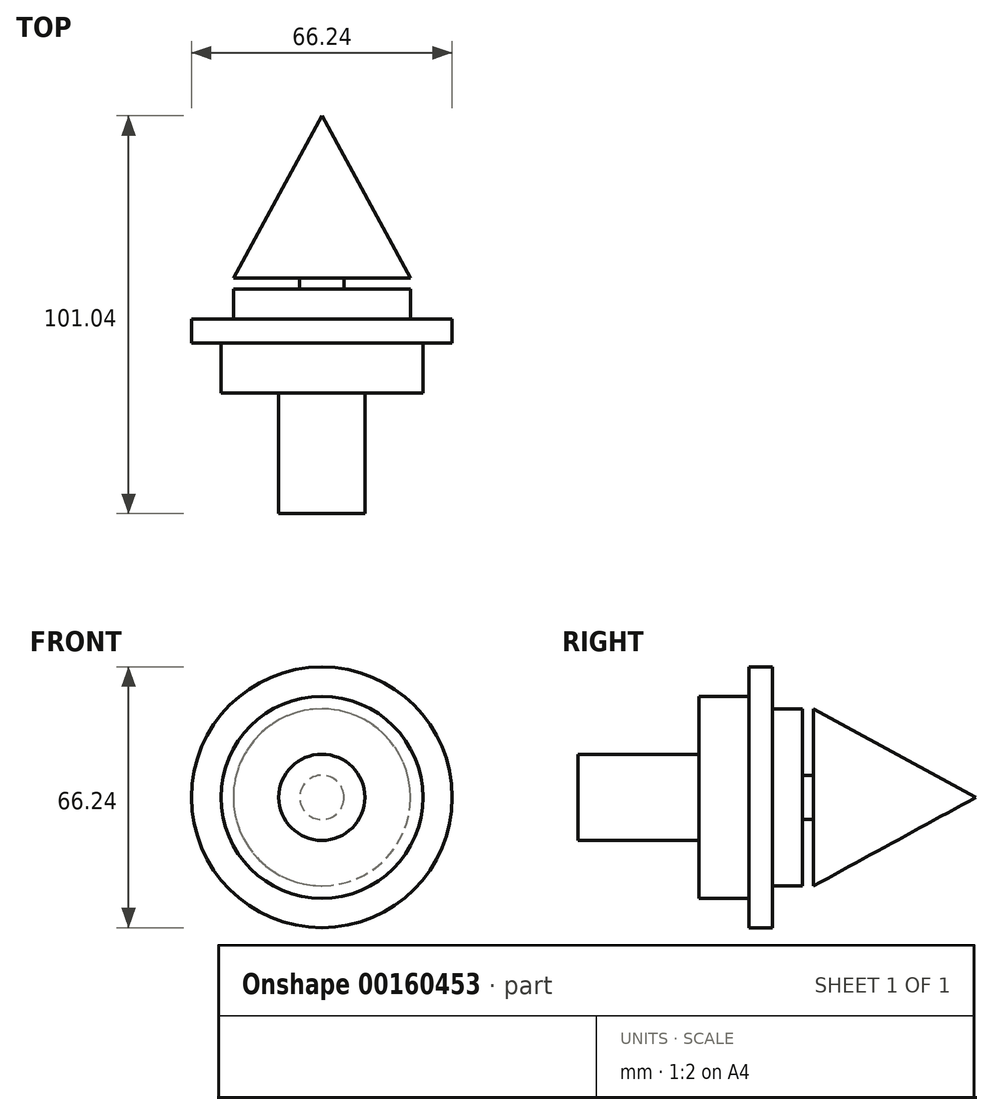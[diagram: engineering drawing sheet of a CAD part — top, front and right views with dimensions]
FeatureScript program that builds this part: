
annotation { "Feature Type Name" : "Feature", "Feature Type Description" : "" }
export const myFeature = defineFeature(function(context is Context, id is Id, definition is map)
    precondition{}
    {
        {
            var Q0;
            Q0=qCreatedBy(makeId("Top.planeOp"),FACE);
            var sketch = newSketch(context, id + "F0", { "sketchPlane" : qUnion([Q0])});
            skLineSegment(sketch, "E0", {"start": v(-33.12, 0) * mm, "end": v(0, 0) * mm});
            skLineSegment(sketch, "E1", {"start": v(-22.5, 0) * mm, "end": v(-22.5, 7.65) * mm});
            skLineSegment(sketch, "E2", {"start": v(-22.5, 7.65) * mm, "end": v(-5.62, 7.65) * mm});
            skLineSegment(sketch, "E3", {"start": v(-5.62, 7.65) * mm, "end": v(-5.62, 10.47) * mm});
            skLineSegment(sketch, "E4", {"start": v(-5.62, 10.47) * mm, "end": v(-22.5, 10.47) * mm});
            skLineSegment(sketch, "E5", {"start": v(-33.12, 0) * mm, "end": v(-33.12, -5.98) * mm});
            skLineSegment(sketch, "E6", {"start": v(-33.12, -5.98) * mm, "end": v(0, -5.98) * mm});
            skLineSegment(sketch, "E7", {"start": v(0, 0) * mm, "end": v(0, -5.98) * mm});
            skPoint(sketch, "E8.MirrorCS.end.orphan", {"position": v(0, -5.98) * mm});
            skPoint(sketch, "E9.orphan", {"position": v(0, 0) * mm});
            skLineSegment(sketch, "E10", {"start": v(-22.5, 10.47) * mm, "end": v(0, 51.7) * mm});
            skLineSegment(sketch, "E11", {"start": v(0, 51.7) * mm, "end": v(0, 0) * mm});
            skSolve(sketch);
        }
        {
            var Q0;
            {var subQ4=sQuery(id+"F0.wireOp",EDGE,"E1");Q0=makeQuery(id+"F0.imprint","IMPRINT",FACE,{"disambiguationData":[TD([[makeQuery(id+"F0.imprint","IMPRINT",EDGE,{"derivedFrom":subQ4}),-1.0]])]});}
            var Q1;
            {var subQ1=sQuery(id+"F0.wireOp",EDGE,"E5");Q1=makeQuery(id+"F0.imprint","IMPRINT",FACE,{"disambiguationData":[TD([[makeQuery(id+"F0.imprint","IMPRINT",EDGE,{"derivedFrom":subQ1}),1.0]])]});}
            var Q2;
            Q2=sQuery(id+"F0.wireOp",EDGE,"E7");
            revolve(context, id + "F1", {"entities" : qUnion([Q0, Q1]), "axis" : qUnion([Q2]), "revolveType" : RevolveType.FULL});
        }
        {
            var Q0;
            Q0=makeQuery(id+"F1.opRevolve","SWEPT_FACE",FACE,{"disambiguationData":[OSD([sQuery(id+"F0.wireOp",EDGE,"E6")])]});
            var sketch = newSketch(context, id + "F2", { "sketchPlane" : qUnion([Q0])});
            skCircle(sketch, "E12", {"center": v(0, 0) * mm, "radius": 10.94 * mm});
            skSolve(sketch);
        }
        {
            var Q0;
            Q0=qCreatedBy(makeId("Top.planeOp"),FACE);
            var sketch = newSketch(context, id + "F3", { "sketchPlane" : qUnion([Q0])});
            skLineSegment(sketch, "E13", {"start": v(0, -6.76) * mm, "end": v(0, -50.12) * mm});
            skSolve(sketch);
        }
        {
            var Q0;
            Q0=makeQuery(id+"F2.imprint","IMPRINT",FACE,{"disambiguationData":[TD([[makeQuery(id+"F2.imprint","IMPRINT",EDGE,{"derivedFrom":sQuery(id+"F2.wireOp",EDGE,"E12")}),1.0]])]});
            var Q1;
            Q1=sQuery(id+"F3.wireOp",EDGE,"E13");
            sweep(context, id + "F4", {"operationType" : NewBodyOperationType.ADD, "profiles" : qUnion([Q0]), "path" : qUnion([Q1])});
        }
        {
            var Q0;
            Q0=makeQuery(id+"F1.opRevolve","SWEPT_FACE",FACE,{"disambiguationData":[OSD([sQuery(id+"F0.wireOp",EDGE,"E6")])]});
            var sketch = newSketch(context, id + "F5", { "sketchPlane" : qUnion([Q0])});
            skCircle(sketch, "E14", {"center": v(0, 0) * mm, "radius": 25.65 * mm});
            skLineSegment(sketch, "E15", {"start": v(0, 25.65) * mm, "end": v(0, 10.94) * mm});
            skLineSegment(sketch, "E16", {"start": v(0, 10.94) * mm, "end": v(10.36, 3.53) * mm});
            skLineSegment(sketch, "E17", {"start": v(0, 10.94) * mm, "end": v(-10.23, 3.88) * mm});
            skLineSegment(sketch, "E18", {"start": v(-10.23, 3.88) * mm, "end": v(-5.38, -9.53) * mm});
            skLineSegment(sketch, "E19", {"start": v(-5.38, -9.53) * mm, "end": v(5.38, -9.53) * mm});
            skLineSegment(sketch, "E20", {"start": v(5.38, -9.53) * mm, "end": v(10.36, 3.53) * mm});
            skSolve(sketch);
        }
        {
            var Q0;
            Q0=makeQuery(id+"F5.imprint","IMPRINT",FACE,{"disambiguationData":[TD([[makeQuery(id+"F5.imprint","IMPRINT",EDGE,{"derivedFrom":sQuery(id+"F5.wireOp",EDGE,"E14")}),1.0]])]});
            extrude(context, id + "F6", {"entities" : qUnion([Q0]), "operationType" : NewBodyOperationType.ADD, "depth" : 12.7 * mm});
        }
        {
            var Q0;
            Q0=sQuery(id+"F5.wireOp",EDGE,"E17");
            var Q1;
            Q1=sQuery(id+"F5.wireOp",EDGE,"E16");
            var Q2;
            Q2=sQuery(id+"F5.wireOp",EDGE,"E20");
            var Q3;
            Q3=sQuery(id+"F5.wireOp",EDGE,"E19");
            var Q4;
            Q4=sQuery(id+"F5.wireOp",EDGE,"E18");
            extrude(context, id + "F7", {"bodyType" : ToolBodyType.SURFACE, "surfaceEntities" : qUnion([Q0, Q1, Q2, Q3, Q4]), "depth" : 76.2 * mm});
        }
        {
            var Q0;
            Q0=makeQuery(id+"F7.opExtrude","SWEPT_EDGE",EDGE,{"disambiguationData":[OSD([sQuery(id+"F5.wireOp",VERTEX,"E19.end")])]});
            var Q1;
            Q1=makeQuery(id+"F7.opExtrude","SWEPT_EDGE",EDGE,{"disambiguationData":[OSD([sQuery(id+"F5.wireOp",VERTEX,"E20.end")])]});
            var Q2;
            Q2=makeQuery(id+"F7.opExtrude","SWEPT_EDGE",EDGE,{"disambiguationData":[OSD([sQuery(id+"F5.wireOp",VERTEX,"E18.start")])]});
            fillet(context, id + "F8", {"entities" : qUnion([Q0, Q1, Q2]), "radius" : 8.64 * mm, "tangentPropagation" : true, "allowEdgeOverflow" : false});
        }
        {
            var Q0;
            Q0=makeQuery(id+"F7.opExtrude","SWEPT_EDGE",EDGE,{"disambiguationData":[OSD([sQuery(id+"F5.wireOp",VERTEX,"E18.end")])]});
            var Q1;
            Q1=makeQuery(id+"F7.opExtrude","SWEPT_EDGE",EDGE,{"disambiguationData":[OSD([sQuery(id+"F5.wireOp",VERTEX,"E16.start")])]});
            fillet(context, id + "F9", {"entities" : qUnion([Q0, Q1]), "radius" : 8.64 * mm, "tangentPropagation" : true, "allowEdgeOverflow" : false});
        }
    });
